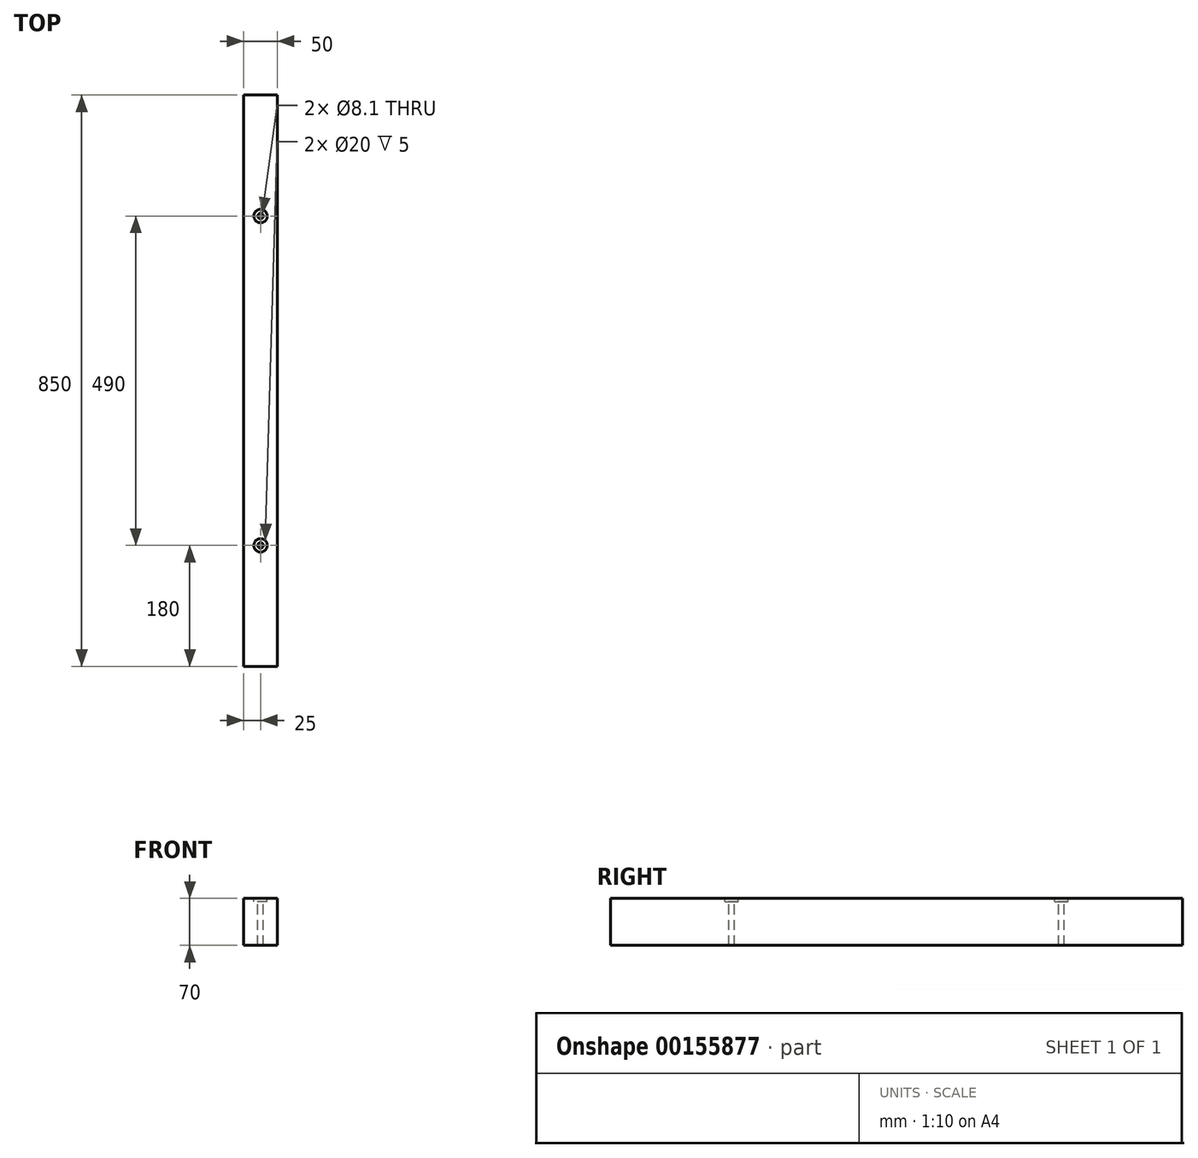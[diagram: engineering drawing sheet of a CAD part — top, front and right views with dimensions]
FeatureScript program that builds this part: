
annotation { "Feature Type Name" : "Feature", "Feature Type Description" : "" }
export const myFeature = defineFeature(function(context is Context, id is Id, definition is map)
    precondition{}
    {
        {
            var Q0;
            Q0=qCreatedBy(makeId("Front.planeOp"),FACE);
            var sketch = newSketch(context, id + "F0", { "sketchPlane" : qUnion([Q0])});
            skLineSegment(sketch, "E0.bottom", {"start": v(25, 35) * mm, "end": v(-25, 35) * mm});
            skLineSegment(sketch, "E0.top", {"start": v(25, -35) * mm, "end": v(-25, -35) * mm});
            skLineSegment(sketch, "E0.left", {"start": v(25, 35) * mm, "end": v(25, -35) * mm});
            skLineSegment(sketch, "E0.right", {"start": v(-25, 35) * mm, "end": v(-25, -35) * mm});
            skPoint(sketch, "E0.middle", {"position": v(0, 0) * mm});
            skSolve(sketch);
        }
        {
            var Q0;
            Q0=makeQuery(id+"F0.imprint","IMPRINT",FACE,{"disambiguationData":[TD([[makeQuery(id+"F0.imprint","IMPRINT",EDGE,{"derivedFrom":sQuery(id+"F0.wireOp",EDGE,"E0.bottom")}),1.0]])]});
            extrude(context, id + "F3", {"entities" : qUnion([Q0]), "depth" : 425 * mm, "hasSecondDirection" : true, "secondDirectionOppositeDirection" : true, "secondDirectionDepth" : 425 * mm});
        }
        {
            var Q0;
            Q0=makeQuery(id+"F3.opExtrude","SWEPT_FACE",FACE,{"disambiguationData":[OSD([sQuery(id+"F0.wireOp",EDGE,"E0.bottom")])]});
            var sketch = newSketch(context, id + "F1", { "sketchPlane" : qUnion([Q0])});
            skPoint(sketch, "E1", {"position": v(0, 245) * mm});
            skPoint(sketch, "E2", {"position": v(0, -245) * mm});
            skSolve(sketch);
        }
        {
            var Q0;
            Q0=sQuery(id+"F1.wireOp",VERTEX,"E2");
            var Q1;
            Q1=sQuery(id+"F1.wireOp",VERTEX,"E1");
            var Q2;
            Q2=makeQuery(id+"F3.opExtrude","SWEPT_BODY",BODY,{"disambiguationData":[OSD([sQuery(id+"F0.wireOp",EDGE,"E0.bottom"),sQuery(id+"F0.wireOp",EDGE,"E0.top"),sQuery(id+"F0.wireOp",EDGE,"E0.left"),sQuery(id+"F0.wireOp",EDGE,"E0.right")])]});
            hole(context, id + "F2", {"style" : HoleStyle.C_BORE, "endStyle" : HoleEndStyle.THROUGH, "holeDiameter" : 8.1 * mm, "cBoreDiameter" : 20 * mm, "cBoreDepth" : 5 * mm, "locations" : qUnion([Q0, Q1]), "scope" : qUnion([Q2]), "isTappedThrough" : true});
        }
    });
